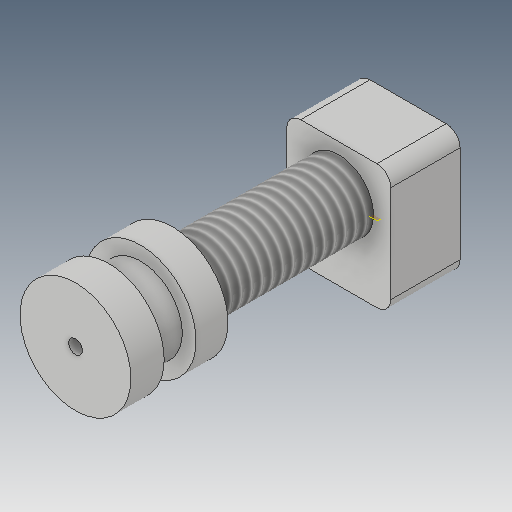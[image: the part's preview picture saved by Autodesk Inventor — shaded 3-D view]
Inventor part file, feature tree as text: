
AUTODESK INVENTOR PART (.ipt)
format: ipt  version: 2017 (Build 210142000, 142)  size: 218,112 bytes
history: native  units: mm
features: sketch x10, extrude x7, projected_geometry x4, other x3, thread x1, plane x1, revolve x1, hole x1, reference x1
ambient origin geometry x8: Origin, YZ Plane, XZ Plane, XY Plane, X Axis, Y Axis, Z Axis, Center Point
bodies: Solid1 (feature_tree)
feature tree (29):
  extrude  "Extrusion1"  Depth=12.0mm
  extrude  "Extrusion2"  Depth=4.6mm TaperAngle=0.0deg
  extrude  "Extrusion3"  Depth=10.0mm TaperAngle=0.0deg
  extrude  "Extrusion4"  Depth=10.0mm
  thread  "Thread1"  [1 undecoded]
  extrude  "Extrusion5"  Depth=10.0mm TaperAngle=0.0deg
  sketch  "Sketch6"  dims[d17=2.3mm d18=-6.622mm]
  plane  "Work Plane1"
  revolve  "Revolution1"  [1 undecoded]
  extrude  "Extrusion6"  TaperAngle=90.0deg  [1 undecoded]
  extrude  "Extrusion7"  Depth=4.75mm TaperAngle=0.0deg
  hole  "Hole1"  [1 undecoded]
  sketch  "Sketch1"  dims[d0=4.8mm d1=0.0mm d2=12.0mm]
  reference  "Reference1"
  sketch  "Sketch2"  dims[d3=4.6mm d4=0.0mm d5=4.6mm d6=0.0mm]
  projected_geometry  "Projected Loop1"
  sketch  "Sketch3"  dims[d7=10.0mm d8=24.0mm d9=0.0mm]
  projected_geometry  "Projected Loop2"
  sketch  "Sketch4"  dims[d10=10.0mm d11=0.0mm d12=15.0mm d13=18.0mm]
  projected_geometry  "Projected Loop3"
  sketch  "Sketch5"  dims[d14=2.0mm d15=10.0mm d16=0.0mm]
  sketch  "Sketch7"  dims[d20=180.0deg d21=90.0deg]
  sketch  "Sketch8"  dims[d22=0.2mm d23=4.75mm d24=0.0mm]
  sketch  "Sketch9"  dims[d25=10.0mm d26=0.0mm]
  sketch  "Sketch10"  dims[d27=2.0mm d28=6.0mm d29=4.0mm d30=2.0mm d31=90.0deg d32=10.0mm d33=20.594885mm]
  projected_geometry  "Projected Loop4"
  other  "<userpath>\OneDrive\Inventor\Beast 3D Printer\Hotend Mount Assembly.iam"
  other  "Hotend Mount Assembly.iam"
  other  "Hotend Clamp P1:1"
note: 4 required parameter values undecoded (feature->parameter linkage not recoverable at this tier; creation-order binding heuristic only, values carry confidence <= 0.55)